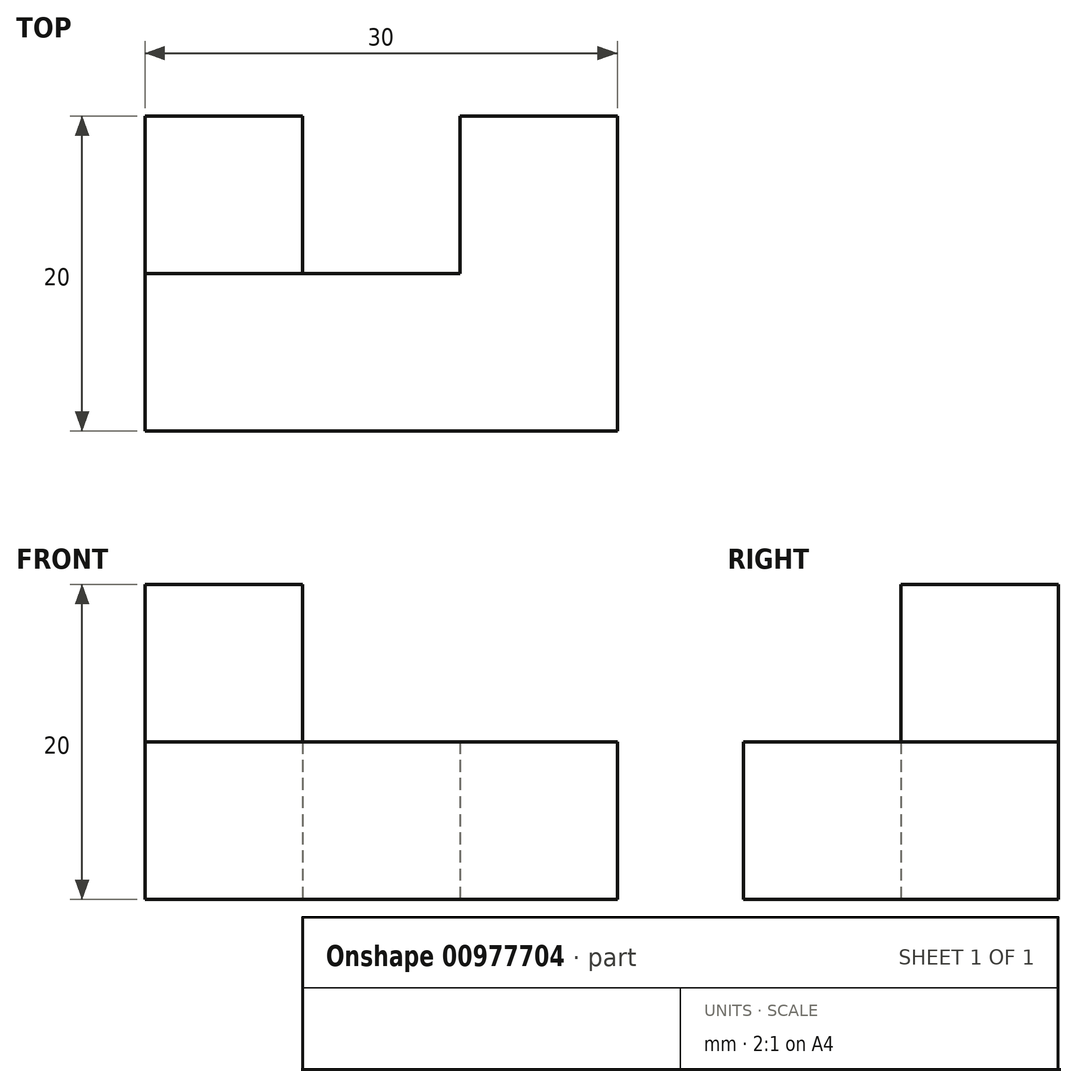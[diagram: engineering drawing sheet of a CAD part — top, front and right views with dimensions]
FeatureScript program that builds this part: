
annotation { "Feature Type Name" : "Feature", "Feature Type Description" : "" }
export const myFeature = defineFeature(function(context is Context, id is Id, definition is map)
    precondition{}
    {
        {
            var Q0;
            Q0=qCreatedBy(makeId("Top.planeOp"),FACE);
            var sketch = newSketch(context, id + "F0", { "sketchPlane" : qUnion([Q0])});
            skLineSegment(sketch, "E0", {"start": v(-16.42, 6.01) * mm, "end": v(-16.42, -13.64) * mm});
            skLineSegment(sketch, "E1", {"start": v(-16.42, -13.64) * mm, "end": v(13.58, -13.64) * mm});
            skLineSegment(sketch, "E2", {"start": v(13.58, -13.64) * mm, "end": v(13.58, 6.36) * mm});
            skLineSegment(sketch, "E3", {"start": v(13.58, 6.36) * mm, "end": v(3.58, 6.36) * mm});
            skLineSegment(sketch, "E4", {"start": v(3.58, 6.36) * mm, "end": v(3.58, -3.64) * mm});
            skLineSegment(sketch, "E5", {"start": v(3.58, -3.64) * mm, "end": v(-6.42, -3.64) * mm});
            skLineSegment(sketch, "E6", {"start": v(-6.42, -3.64) * mm, "end": v(-6.42, 6.36) * mm});
            skLineSegment(sketch, "E7", {"start": v(-6.42, 6.36) * mm, "end": v(-16.42, 6.36) * mm});
            skLineSegment(sketch, "E8", {"start": v(-16.42, 6.01) * mm, "end": v(-16.42, 6.36) * mm});
            skSolve(sketch);
        }
        {
            var Q0;
            Q0=makeQuery(id+"F0.imprint","IMPRINT",FACE,{"disambiguationData":[TD([[makeQuery(id+"F0.imprint","IMPRINT",EDGE,{"derivedFrom":sQuery(id+"F0.wireOp",EDGE,"E0")}),1.0]])]});
            extrude(context, id + "F1", {"entities" : qUnion([Q0]), "depth" : 10 * mm, "offsetDistance" : 25 * mm});
        }
        {
            var Q0;
            Q0=makeQuery(id+"F1.opExtrude","CAP_FACE",FACE,{"disambiguationData":[OSD([sQuery(id+"F0.wireOp",EDGE,"E0"),sQuery(id+"F0.wireOp",EDGE,"E1"),sQuery(id+"F0.wireOp",EDGE,"E2"),sQuery(id+"F0.wireOp",EDGE,"E3"),sQuery(id+"F0.wireOp",EDGE,"E4"),sQuery(id+"F0.wireOp",EDGE,"E5"),sQuery(id+"F0.wireOp",EDGE,"E6"),sQuery(id+"F0.wireOp",EDGE,"E7"),sQuery(id+"F0.wireOp",EDGE,"E8")])],"isStart":false});
            var sketch = newSketch(context, id + "F2", { "sketchPlane" : qUnion([Q0])});
            skLineSegment(sketch, "E9", {"start": v(-6.42, -3.64) * mm, "end": v(-16.42, -3.64) * mm});
            skLineSegment(sketch, "E10", {"start": v(-16.42, -3.64) * mm, "end": v(-16.42, 6.36) * mm});
            skLineSegment(sketch, "E11", {"start": v(-16.42, 6.36) * mm, "end": v(-6.42, 6.36) * mm});
            skLineSegment(sketch, "E12", {"start": v(-6.42, 6.36) * mm, "end": v(-6.42, -3.64) * mm});
            skSolve(sketch);
        }
        {
            var Q0;
            Q0=makeQuery(id+"F2.imprint","IMPRINT",FACE,{"disambiguationData":[TD([[makeQuery(id+"F2.imprint","IMPRINT",EDGE,{"derivedFrom":sQuery(id+"F2.wireOp",EDGE,"E9")}),-1.0]])]});
            extrude(context, id + "F3", {"entities" : qUnion([Q0]), "operationType" : NewBodyOperationType.ADD, "depth" : 10 * mm, "offsetDistance" : 25 * mm});
        }
    });
